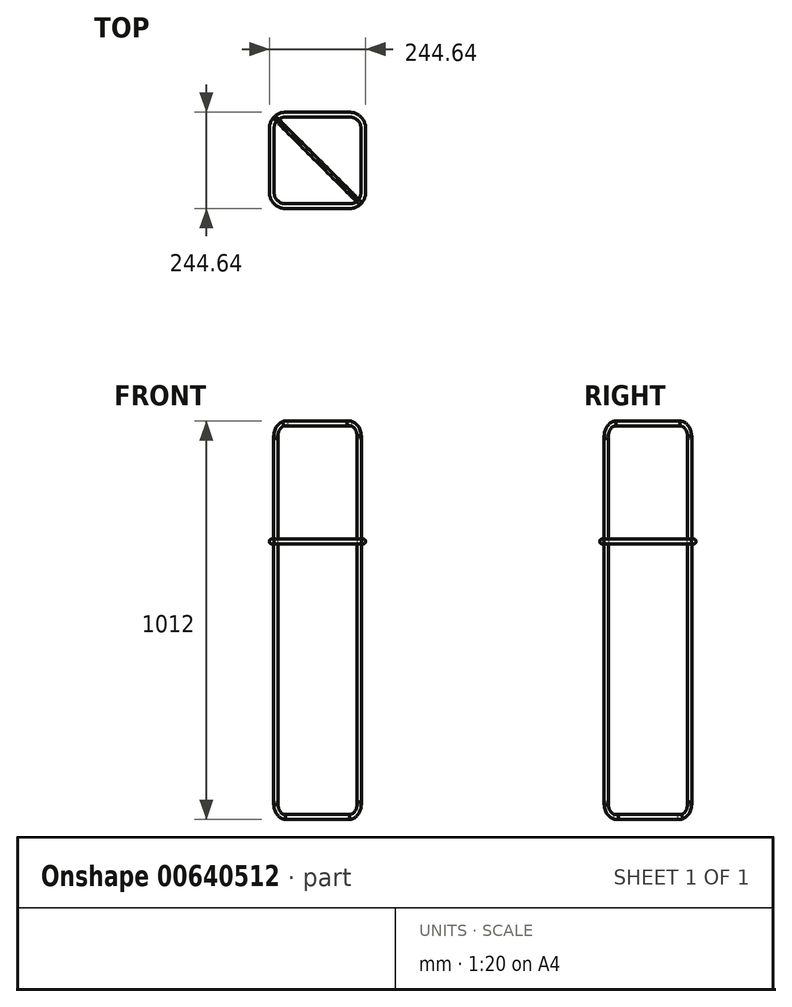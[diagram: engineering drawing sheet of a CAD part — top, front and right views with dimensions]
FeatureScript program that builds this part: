
annotation { "Feature Type Name" : "Feature", "Feature Type Description" : "" }
export const myFeature = defineFeature(function(context is Context, id is Id, definition is map)
    precondition{}
    {
        {
            var Q0;
            Q0=qCreatedBy(makeId("Front.planeOp"),FACE);
            var sketch = newSketch(context, id + "F0", { "sketchPlane" : qUnion([Q0])});
            skLineSegment(sketch, "E0", {"start": v(0, 0) * mm, "end": v(0, 1000) * mm, "construction": true});
            skSolve(sketch);
        }
        {
            var Q0;
            Q0=sQuery(id+"F0.wireOp",EDGE,"E0");
            cPlane(context, id + "F1", {"entities" : qUnion([Q0]), "cplaneType" : CPlaneType.LINE_ANGLE, "offset" : 25 * mm, "angle" : 45 * degree, "width" : 150 * mm, "height" : 150 * mm});
        }
        {
            var Q0;
            Q0=qCreatedBy(id+"F1.planeOp",FACE);
            var sketch = newSketch(context, id + "F2", { "sketchPlane" : qUnion([Q0])});
            skLineSegment(sketch, "E1.bottom", {"start": v(150, 0) * mm, "end": v(-150, 0) * mm, "construction": true});
            skLineSegment(sketch, "E1.top", {"start": v(150, 1000) * mm, "end": v(-150, 1000) * mm, "construction": true});
            skLineSegment(sketch, "E1.left", {"start": v(150, 0) * mm, "end": v(150, 1000) * mm, "construction": true});
            skLineSegment(sketch, "E1.right", {"start": v(-150, 0) * mm, "end": v(-150, 1000) * mm, "construction": true});
            skPoint(sketch, "E1.middle", {"position": v(0, 500) * mm});
            skLineSegment(sketch, "E2.bottom", {"start": v(-115, 1000) * mm, "end": v(115, 1000) * mm});
            skLineSegment(sketch, "E2.top", {"start": v(-115, 0) * mm, "end": v(115, 0) * mm});
            skLineSegment(sketch, "E2.left", {"start": v(-150, 965) * mm, "end": v(-150, 35) * mm});
            skLineSegment(sketch, "E2.right", {"start": v(150, 965) * mm, "end": v(150, 35) * mm});
            skPoint(sketch, "E3.visualSharp", {"position": v(-150, 1000) * mm});
            skArc(sketch, "E3.filletArc", {"start": v(-115, 1000) * mm, "mid": v(-139.75, 989.75) * mm, "end": v(-150, 965) * mm});
            skPoint(sketch, "E4.visualSharp", {"position": v(150, 1000) * mm});
            skArc(sketch, "E4.filletArc", {"start": v(150, 965) * mm, "mid": v(139.75, 989.75) * mm, "end": v(115, 1000) * mm});
            skPoint(sketch, "E5.visualSharp", {"position": v(150, 0) * mm});
            skArc(sketch, "E5.filletArc", {"start": v(115, 0) * mm, "mid": v(139.75, 10.25) * mm, "end": v(150, 35) * mm});
            skPoint(sketch, "E6.visualSharp", {"position": v(-150, 0) * mm});
            skArc(sketch, "E6.filletArc", {"start": v(-150, 35) * mm, "mid": v(-139.75, 10.25) * mm, "end": v(-115, 0) * mm});
            skLineSegment(sketch, "E7", {"start": v(0, 1000) * mm, "end": v(0, 700) * mm, "construction": true});
            skSolve(sketch);
        }
        {
            var Q0;
            Q0=qCreatedBy(makeId("Right.planeOp"),FACE);
            var sketch = newSketch(context, id + "F3", { "sketchPlane" : qUnion([Q0])});
            skCircle(sketch, "E8", {"center": v(0, 0) * mm, "radius": 6 * mm});
            skSolve(sketch);
        }
        {
            var Q0;
            Q0 = qSketchRegion(id + "F3", true);
            var Q1;
            Q1=sQuery(id+"F2.wireOp",EDGE,"E6.filletArc");
            var Q2;
            Q2=sQuery(id+"F2.wireOp",EDGE,"E2.top");
            var Q3;
            Q3=sQuery(id+"F2.wireOp",EDGE,"E2.left");
            var Q4;
            Q4=sQuery(id+"F2.wireOp",EDGE,"E3.filletArc");
            var Q5;
            Q5=sQuery(id+"F2.wireOp",EDGE,"E2.bottom");
            var Q6;
            Q6=sQuery(id+"F2.wireOp",EDGE,"E4.filletArc");
            var Q7;
            Q7=sQuery(id+"F2.wireOp",EDGE,"E2.right");
            var Q8;
            Q8=sQuery(id+"F2.wireOp",EDGE,"E5.filletArc");
            sweep(context, id + "F4", {"profiles" : qUnion([Q0]), "path" : qUnion([Q1, Q2, Q3, Q4, Q5, Q6, Q7, Q8])});
        }
        {
            var Q0;
            Q0=sQuery(id+"F2.wireOp",VERTEX,"E7.end");
            var Q1;
            Q1=qCreatedBy(makeId("Top.planeOp"),FACE);
            cPlane(context, id + "F5", {"entities" : qUnion([Q0, Q1]), "cplaneType" : CPlaneType.PLANE_POINT, "offset" : 25 * mm, "width" : 150 * mm, "height" : 150 * mm});
        }
        {
            var Q0;
            Q0=qCreatedBy(id+"F5.planeOp",FACE);
            var sketch = newSketch(context, id + "F6", { "sketchPlane" : qUnion([Q0])});
            skLineSegment(sketch, "E9.bottom", {"start": v(81.32, -116.32) * mm, "end": v(-81.32, -116.32) * mm});
            skLineSegment(sketch, "E9.top", {"start": v(81.32, 116.32) * mm, "end": v(-81.32, 116.32) * mm});
            skLineSegment(sketch, "E9.left", {"start": v(116.32, -81.32) * mm, "end": v(116.32, 81.32) * mm});
            skLineSegment(sketch, "E9.right", {"start": v(-116.32, -81.32) * mm, "end": v(-116.32, 81.32) * mm});
            skPoint(sketch, "E9.middle", {"position": v(0, 0) * mm});
            skPoint(sketch, "E10.visualSharp", {"position": v(-116.32, 116.32) * mm});
            skArc(sketch, "E10.filletArc", {"start": v(-81.32, 116.32) * mm, "mid": v(-106.07, 106.07) * mm, "end": v(-116.32, 81.32) * mm});
            skPoint(sketch, "E11.visualSharp", {"position": v(116.32, 116.32) * mm});
            skArc(sketch, "E11.filletArc", {"start": v(116.32, 81.32) * mm, "mid": v(106.07, 106.07) * mm, "end": v(81.32, 116.32) * mm});
            skPoint(sketch, "E12.visualSharp", {"position": v(116.32, -116.32) * mm});
            skArc(sketch, "E12.filletArc", {"start": v(81.32, -116.32) * mm, "mid": v(106.07, -106.07) * mm, "end": v(116.32, -81.32) * mm});
            skPoint(sketch, "E13.visualSharp", {"position": v(-116.32, -116.32) * mm});
            skArc(sketch, "E13.filletArc", {"start": v(-116.32, -81.32) * mm, "mid": v(-106.07, -106.07) * mm, "end": v(-81.32, -116.32) * mm});
            skPoint(sketch, "E14", {"position": v(106.07, -106.07) * mm});
            skSolve(sketch);
        }
        {
            var Q0;
            Q0=qCreatedBy(makeId("Front.planeOp"),FACE);
            var sketch = newSketch(context, id + "F7", { "sketchPlane" : qUnion([Q0])});
            skCircle(sketch, "E15", {"center": v(116.32, 700) * mm, "radius": 6 * mm});
            skSolve(sketch);
        }
        {
            var Q0;
            Q0 = qSketchRegion(id + "F7", true);
            var Q1;
            Q1=sQuery(id+"F6.wireOp",EDGE,"E9.left");
            var Q2;
            Q2=sQuery(id+"F6.wireOp",EDGE,"E12.filletArc");
            var Q3;
            Q3=sQuery(id+"F6.wireOp",EDGE,"E9.bottom");
            var Q4;
            Q4=sQuery(id+"F6.wireOp",EDGE,"E13.filletArc");
            var Q5;
            Q5=sQuery(id+"F6.wireOp",EDGE,"E9.right");
            var Q6;
            Q6=sQuery(id+"F6.wireOp",EDGE,"E10.filletArc");
            var Q7;
            Q7=sQuery(id+"F6.wireOp",EDGE,"E9.top");
            var Q8;
            Q8=sQuery(id+"F6.wireOp",EDGE,"E11.filletArc");
            sweep(context, id + "F8", {"profiles" : qUnion([Q0]), "path" : qUnion([Q1, Q2, Q3, Q4, Q5, Q6, Q7, Q8])});
        }
    });
